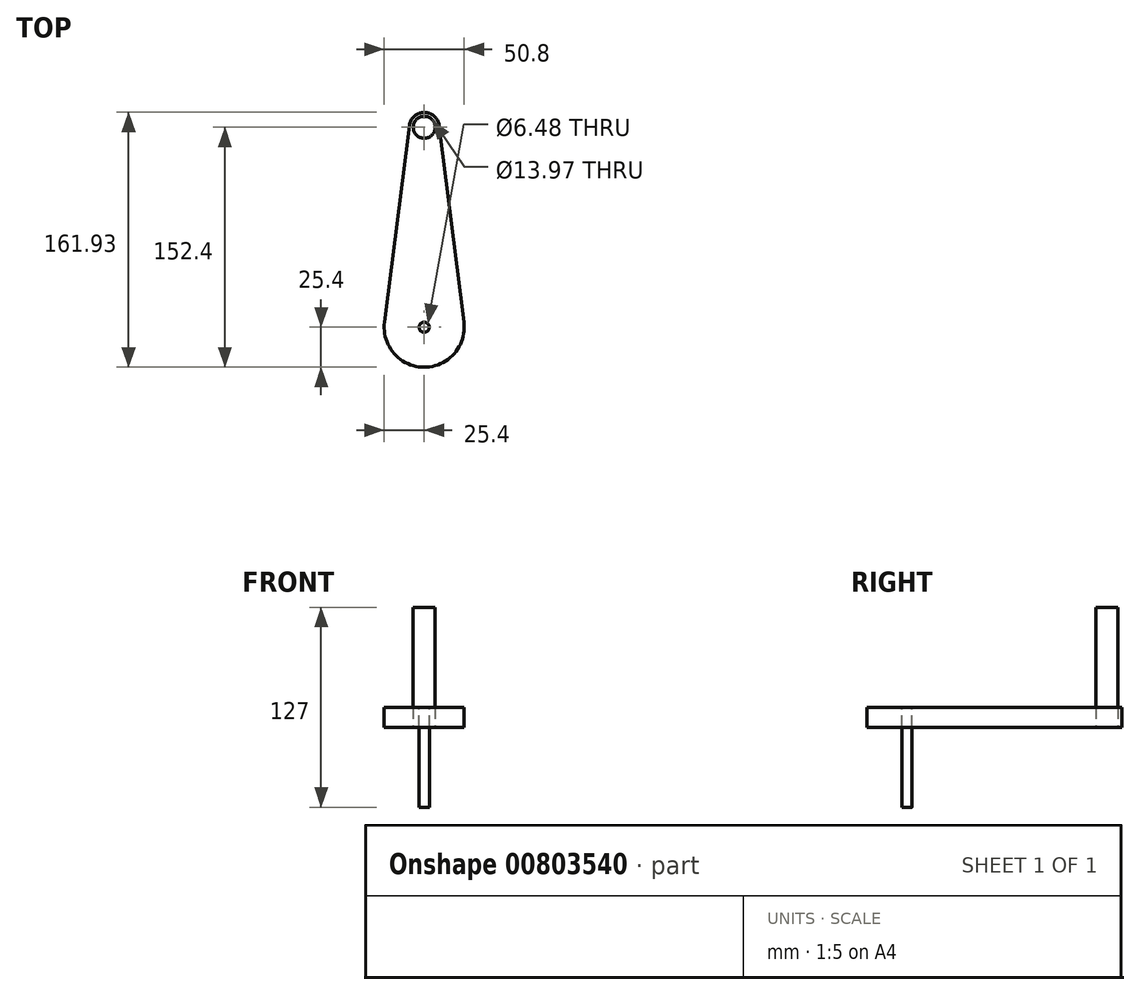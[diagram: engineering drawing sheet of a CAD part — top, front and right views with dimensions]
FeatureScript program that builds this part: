
annotation { "Feature Type Name" : "Feature", "Feature Type Description" : "" }
export const myFeature = defineFeature(function(context is Context, id is Id, definition is map)
    precondition{}
    {
        {
            var Q0;
            Q0=qCreatedBy(makeId("Top.planeOp"),FACE);
            var sketch = newSketch(context, id + "F0", { "sketchPlane" : qUnion([Q0])});
            skCircle(sketch, "E0", {"center": v(0, 0) * mm, "radius": 25.4 * mm});
            skCircle(sketch, "E1", {"center": v(0, 127) * mm, "radius": 9.53 * mm});
            skLineSegment(sketch, "E2", {"start": v(9.45, 128.2) * mm, "end": v(25.2, 3.18) * mm});
            skLineSegment(sketch, "E3", {"start": v(-9.45, 128.2) * mm, "end": v(-25.2, 3.18) * mm});
            skCircle(sketch, "E4", {"center": v(0, 0) * mm, "radius": 3.24 * mm});
            skCircle(sketch, "E5", {"center": v(0, 127) * mm, "radius": 6.99 * mm});
            skSolve(sketch);
        }
        {
            var Q0;
            Q0=makeQuery(id+"F0.imprint","IMPRINT",FACE,{"disambiguationData":[TD([[makeQuery(id+"F0.imprint","IMPRINT",EDGE,{"derivedFrom":sQuery(id+"F0.wireOp",EDGE,"E5")}),1.0]])]});
            var Q1;
            Q1=makeQuery(id+"F0.imprint","IMPRINT",FACE,{"disambiguationData":[TD([[makeQuery(id+"F0.imprint","IMPRINT",EDGE,{"derivedFrom":sQuery(id+"F0.wireOp",EDGE,"E5")}),1.0]])]});
            extrude(context, id + "F1", {"entities" : qUnion([Q0, Q1]), "depth" : 76.2 * mm, "offsetDistance" : 25.4 * mm});
        }
        {
            var Q0;
            Q0=makeQuery(id+"F0.imprint","IMPRINT",FACE,{"disambiguationData":[TD([[makeQuery(id+"F0.imprint","IMPRINT",EDGE,{"derivedFrom":sQuery(id+"F0.wireOp",EDGE,"E4")}),1.0]])]});
            extrude(context, id + "F2", {"entities" : qUnion([Q0]), "oppositeDirection" : true, "depth" : 50.8 * mm, "offsetDistance" : 25.4 * mm});
        }
        {
            var Q0;
            Q0=makeQuery(id+"F2.opExtrude","CAP_FACE",FACE,{"disambiguationData":[OSD([sQuery(id+"F0.wireOp",EDGE,"E4")])],"isStart":true});
            var Q1;
            Q1=makeQuery(id+"F2.opExtrude","CAP_FACE",FACE,{"disambiguationData":[OSD([sQuery(id+"F0.wireOp",EDGE,"E4")])],"isStart":true});
            extrude(context, id + "F3", {"entities" : qUnion([Q0, Q1]), "operationType" : NewBodyOperationType.ADD, "depth" : 12.7 * mm, "offsetDistance" : 25.4 * mm});
        }
        {
            var Q0;
            Q0=makeQuery(id+"F0.imprint","IMPRINT",FACE,{"disambiguationData":[TD([[makeQuery(id+"F0.imprint","IMPRINT",EDGE,{"derivedFrom":sQuery(id+"F0.wireOp",EDGE,"E4")}),-1.0]])]});
            var Q1;
            {var subQ0=sQuery(id+"F0.wireOp",EDGE,"E2");Q1=makeQuery(id+"F0.imprint","IMPRINT",FACE,{"disambiguationData":[TD([[makeQuery(id+"F0.imprint","IMPRINT",EDGE,{"derivedFrom":subQ0}),-1.0]])]});}
            var Q2;
            Q2=makeQuery(id+"F0.imprint","IMPRINT",FACE,{"disambiguationData":[TD([[makeQuery(id+"F0.imprint","IMPRINT",EDGE,{"derivedFrom":sQuery(id+"F0.wireOp",EDGE,"E5")}),-1.0]])]});
            extrude(context, id + "F4", {"entities" : qUnion([Q0, Q1, Q2]), "depth" : 12.7 * mm, "offsetDistance" : 25.4 * mm});
        }
    });
